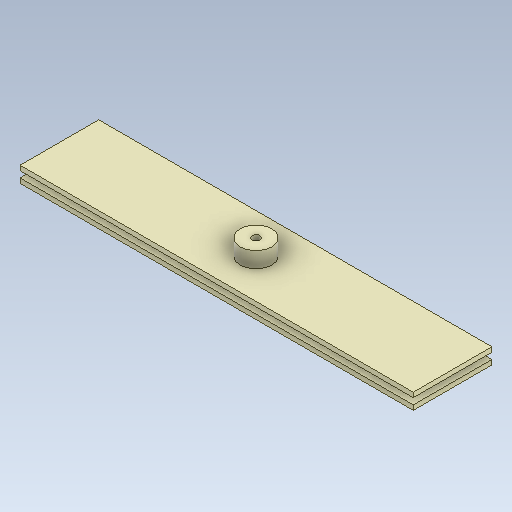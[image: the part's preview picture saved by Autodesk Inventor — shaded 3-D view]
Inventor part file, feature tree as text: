
AUTODESK INVENTOR PART (.ipt)
format: ipt  version: 2020.2 (Build 242310000, 310)  size: 125,440 bytes
history: native  units: in
note: dims shown in document units (in); Inventor stores cm internally (conversion verified against a paired STEP export)
features: extrude x5, sketch x5
ambient origin geometry x8: Origin, YZ Plane, XZ Plane, XY Plane, X Axis, Y Axis, Z Axis, Center Point
bodies: Solid1 (feature_tree)
feature tree (10):
  extrude  "Extrusion1"  Depth=1.9685in
  extrude  "Extrusion2"  Depth=9.4488in
  extrude  "Extrusion3"  Depth=0.1575in TaperAngle=0.0deg
  extrude  "Extrusion4"  Depth=0.7874in
  extrude  "Extrusion5"  Depth=0.1969in
  sketch  "Sketch1"  dims[d0=9.8425in d1=1.9685in]
  sketch  "Sketch2"  dims[d2=0.1181in d3=0.0in d4=9.4488in]
  sketch  "Sketch3"  dims[d5=1.5748in d6=0.1575in d7=0.0in]
  sketch  "Sketch4"  dims[d8=0.1181in d9=0.0in d10=0.7874in]
  sketch  "Sketch5"  dims[d11=0.3937in d12=0.0in d13=0.1969in d14=1.1811in d15=0.0in]
